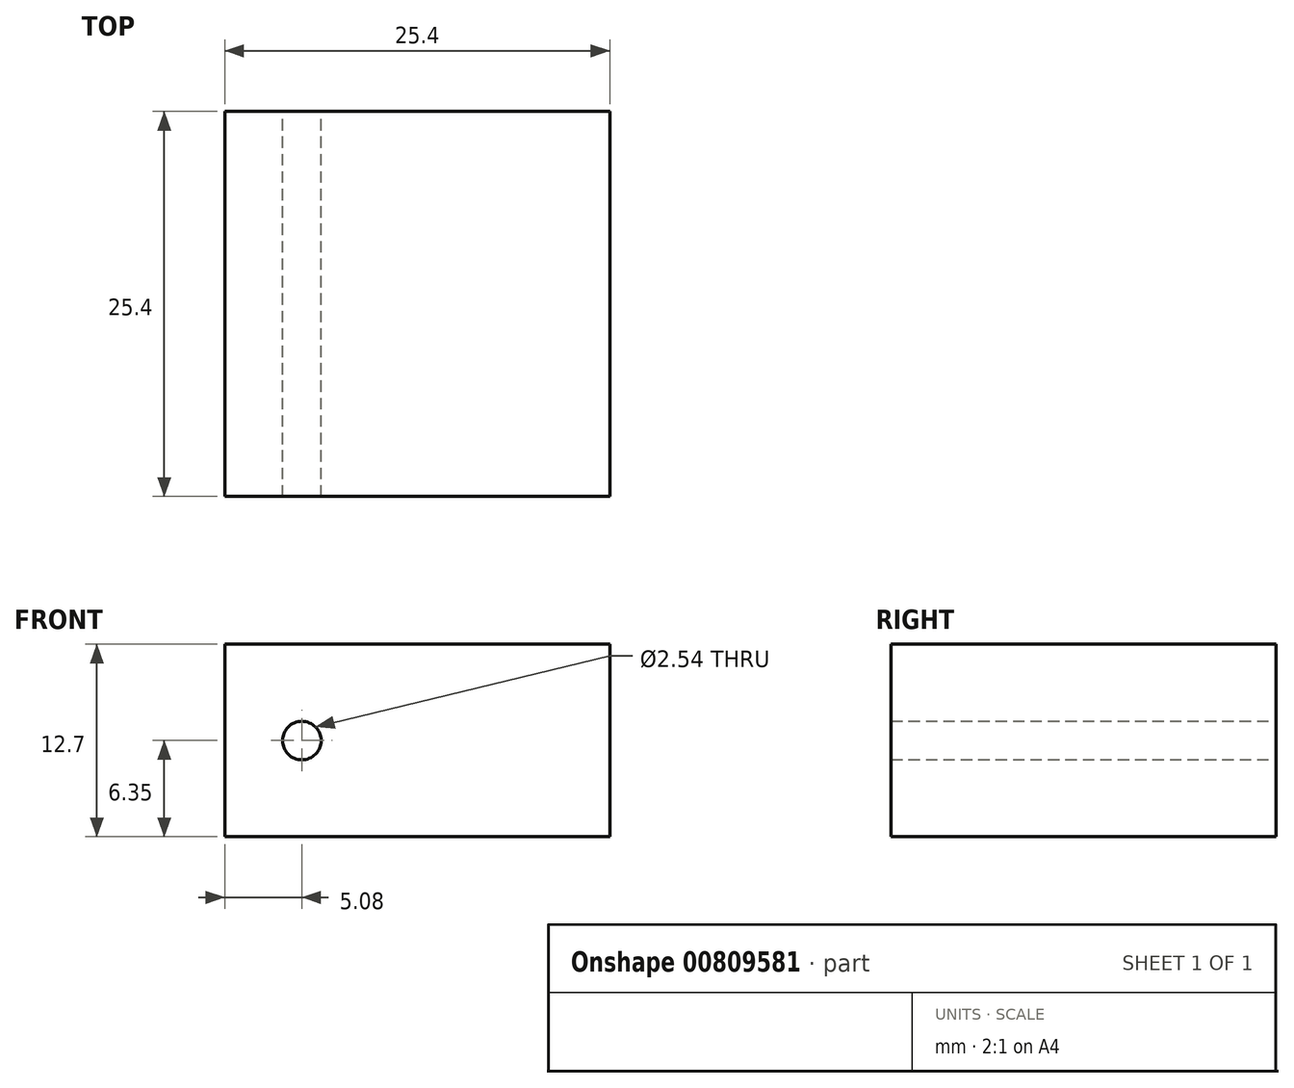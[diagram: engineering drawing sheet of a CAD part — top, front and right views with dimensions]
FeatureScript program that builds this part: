
annotation { "Feature Type Name" : "Feature", "Feature Type Description" : "" }
export const myFeature = defineFeature(function(context is Context, id is Id, definition is map)
    precondition{}
    {
        {
            var Q0;
            Q0=qCreatedBy(makeId("Front.planeOp"),FACE);
            var sketch = newSketch(context, id + "F0", { "sketchPlane" : qUnion([Q0])});
            skLineSegment(sketch, "E0.bottom", {"start": v(12.7, -6.35) * mm, "end": v(-12.7, -6.35) * mm});
            skLineSegment(sketch, "E0.top", {"start": v(12.7, 6.35) * mm, "end": v(-12.7, 6.35) * mm});
            skLineSegment(sketch, "E0.left", {"start": v(12.7, -6.35) * mm, "end": v(12.7, 6.35) * mm});
            skLineSegment(sketch, "E0.right", {"start": v(-12.7, -6.35) * mm, "end": v(-12.7, 6.35) * mm});
            skPoint(sketch, "E0.middle", {"position": v(0, 0) * mm});
            skCircle(sketch, "E1", {"center": v(-7.62, 0) * mm, "radius": 1.27 * mm});
            skSolve(sketch);
        }
        {
            var Q0;
            Q0 = qSketchRegion(id + "F0", true);
            extrude(context, id + "F1", {"entities" : qUnion([Q0]), "depth" : 25.4 * mm, "offsetDistance" : 25.4 * mm});
        }
    });
